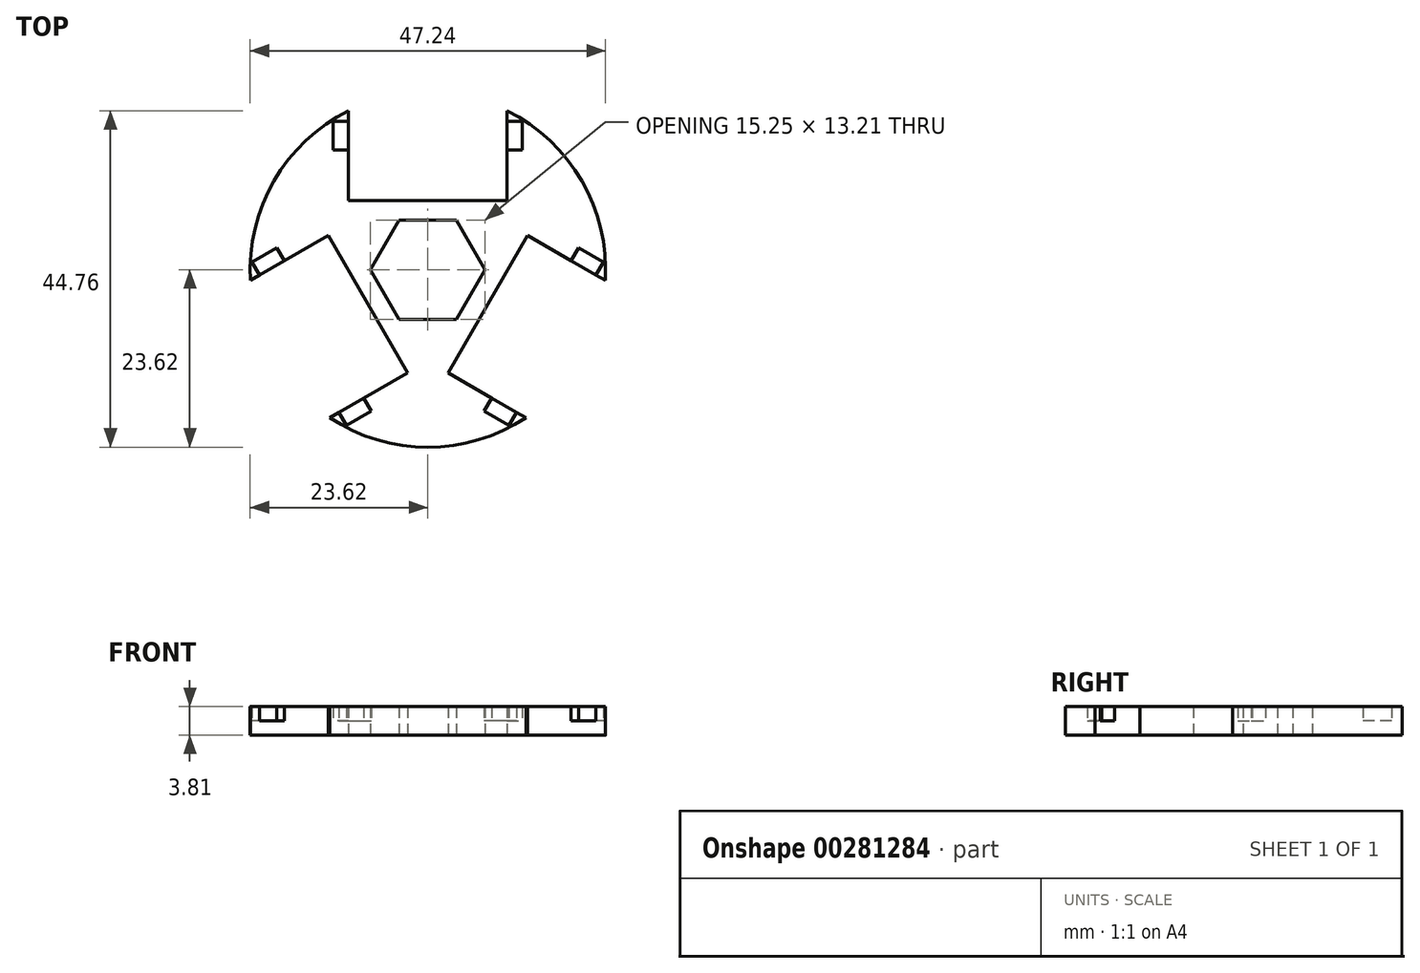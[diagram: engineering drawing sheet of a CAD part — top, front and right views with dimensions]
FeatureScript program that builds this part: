
annotation { "Feature Type Name" : "Feature", "Feature Type Description" : "" }
export const myFeature = defineFeature(function(context is Context, id is Id, definition is map)
    precondition{}
    {
        {
            var Q0;
            Q0=qCreatedBy(makeId("Top.planeOp"),FACE);
            var sketch = newSketch(context, id + "F0", { "sketchPlane" : qUnion([Q0])});
            skCircle(sketch, "E0.cCircle", {"center": v(0, 0) * mm, "radius": 6.6 * mm, "construction": true});
            skLineSegment(sketch, "E0.0", {"start": v(-3.81, 6.6) * mm, "end": v(3.81, 6.6) * mm});
            skLineSegment(sketch, "E0.1", {"start": v(3.81, 6.6) * mm, "end": v(7.63, 0) * mm});
            skLineSegment(sketch, "E0.2", {"start": v(7.63, 0) * mm, "end": v(3.81, -6.6) * mm});
            skLineSegment(sketch, "E0.3", {"start": v(3.81, -6.6) * mm, "end": v(-3.81, -6.6) * mm});
            skLineSegment(sketch, "E0.4", {"start": v(-3.81, -6.6) * mm, "end": v(-7.63, 0) * mm});
            skLineSegment(sketch, "E0.5", {"start": v(-7.63, 0) * mm, "end": v(-3.81, 6.6) * mm});
            skPoint(sketch, "E0.0.midPoint", {"position": v(0, 6.6) * mm});
            skCircle(sketch, "E1", {"center": v(0, 0) * mm, "radius": 23.62 * mm});
            skLineSegment(sketch, "E2.bottom", {"start": v(-10.54, 21.14) * mm, "end": v(10.54, 21.14) * mm});
            skLineSegment(sketch, "E2.top", {"start": v(-10.54, 9.2) * mm, "end": v(10.54, 9.2) * mm});
            skPoint(sketch, "E3.endSnap0", {"position": v(0, 21.14) * mm});
            skLineSegment(sketch, "E4.bottom", {"start": v(-10.54, 19.72) * mm, "end": v(-12.57, 19.72) * mm});
            skLineSegment(sketch, "E4.top", {"start": v(-10.54, 15.9) * mm, "end": v(-12.57, 15.9) * mm});
            skLineSegment(sketch, "E4.right", {"start": v(-12.57, 19.72) * mm, "end": v(-12.57, 15.9) * mm});
            skLineSegment(sketch, "E5", {"start": v(10.54, 21.14) * mm, "end": v(10.54, 19.72) * mm});
            skLineSegment(sketch, "E6", {"start": v(10.54, 15.9) * mm, "end": v(10.54, 9.2) * mm});
            skLineSegment(sketch, "E7", {"start": v(-10.54, 19.72) * mm, "end": v(-10.54, 21.14) * mm});
            skLineSegment(sketch, "E8", {"start": v(-10.54, 15.9) * mm, "end": v(-10.54, 9.2) * mm});
            skLineSegment(sketch, "E9.bottom", {"start": v(10.54, 19.72) * mm, "end": v(12.57, 19.72) * mm});
            skLineSegment(sketch, "E9.top", {"start": v(10.54, 15.9) * mm, "end": v(12.57, 15.9) * mm});
            skLineSegment(sketch, "E9.right", {"start": v(12.57, 19.72) * mm, "end": v(12.57, 15.9) * mm});
            skLineSegment(sketch, "E10", {"start": v(-10.54, 15.9) * mm, "end": v(-10.54, 19.72) * mm});
            skLineSegment(sketch, "E11", {"start": v(10.54, 19.72) * mm, "end": v(10.54, 15.9) * mm});
            skPoint(sketch, "E12", {"position": v(15.71, 9.07) * mm});
            skLineSegment(sketch, "E13.1.0", {"start": v(-22.35, -0.73) * mm, "end": v(-23.36, 1.03) * mm});
            skLineSegment(sketch, "E13.1.1", {"start": v(-23.36, 1.03) * mm, "end": v(-20.06, 2.94) * mm});
            skLineSegment(sketch, "E13.1.2", {"start": v(-22.35, -0.73) * mm, "end": v(-19.05, 1.18) * mm});
            skLineSegment(sketch, "E13.1.3", {"start": v(-19.05, 1.18) * mm, "end": v(-20.06, 2.94) * mm});
            skLineSegment(sketch, "E13.1.4", {"start": v(-19.05, 1.18) * mm, "end": v(-13.24, 4.53) * mm});
            skLineSegment(sketch, "E13.1.5", {"start": v(-2.7, -13.73) * mm, "end": v(-13.24, 4.53) * mm});
            skLineSegment(sketch, "E13.1.6", {"start": v(-8.5, -17.08) * mm, "end": v(-2.7, -13.73) * mm});
            skLineSegment(sketch, "E13.1.7", {"start": v(-8.5, -17.08) * mm, "end": v(-7.49, -18.84) * mm});
            skLineSegment(sketch, "E13.1.8", {"start": v(-8.5, -17.08) * mm, "end": v(-11.8, -18.99) * mm});
            skLineSegment(sketch, "E13.1.9", {"start": v(-11.8, -18.99) * mm, "end": v(-10.79, -20.75) * mm});
            skLineSegment(sketch, "E13.1.10", {"start": v(-10.79, -20.75) * mm, "end": v(-7.49, -18.84) * mm});
            skLineSegment(sketch, "E13.1.11", {"start": v(-11.8, -18.99) * mm, "end": v(-13.04, -19.7) * mm});
            skLineSegment(sketch, "E13.1.12", {"start": v(-13.04, -19.7) * mm, "end": v(-23.58, -1.44) * mm});
            skLineSegment(sketch, "E13.1.13", {"start": v(-23.58, -1.44) * mm, "end": v(-22.35, -0.73) * mm});
            skPoint(sketch, "E13.1.14", {"position": v(-15.71, 9.07) * mm});
            skLineSegment(sketch, "E13.2.0", {"start": v(11.8, -18.99) * mm, "end": v(10.79, -20.75) * mm});
            skLineSegment(sketch, "E13.2.1", {"start": v(10.79, -20.75) * mm, "end": v(7.49, -18.84) * mm});
            skLineSegment(sketch, "E13.2.2", {"start": v(11.8, -18.99) * mm, "end": v(8.5, -17.08) * mm});
            skLineSegment(sketch, "E13.2.3", {"start": v(8.5, -17.08) * mm, "end": v(7.49, -18.84) * mm});
            skLineSegment(sketch, "E13.2.4", {"start": v(8.5, -17.08) * mm, "end": v(2.7, -13.73) * mm});
            skLineSegment(sketch, "E13.2.5", {"start": v(13.24, 4.53) * mm, "end": v(2.7, -13.73) * mm});
            skLineSegment(sketch, "E13.2.6", {"start": v(19.05, 1.18) * mm, "end": v(13.24, 4.53) * mm});
            skLineSegment(sketch, "E13.2.7", {"start": v(19.05, 1.18) * mm, "end": v(20.06, 2.94) * mm});
            skLineSegment(sketch, "E13.2.8", {"start": v(19.05, 1.18) * mm, "end": v(22.35, -0.73) * mm});
            skLineSegment(sketch, "E13.2.9", {"start": v(22.35, -0.73) * mm, "end": v(23.36, 1.03) * mm});
            skLineSegment(sketch, "E13.2.10", {"start": v(23.36, 1.03) * mm, "end": v(20.06, 2.94) * mm});
            skLineSegment(sketch, "E13.2.11", {"start": v(22.35, -0.73) * mm, "end": v(23.58, -1.44) * mm});
            skLineSegment(sketch, "E13.2.12", {"start": v(23.58, -1.44) * mm, "end": v(13.04, -19.7) * mm});
            skLineSegment(sketch, "E13.2.13", {"start": v(13.04, -19.7) * mm, "end": v(11.8, -18.99) * mm});
            skPoint(sketch, "E13.2.14", {"position": v(0, -18.14) * mm});
            skCircle(sketch, "E14.cCircle", {"center": v(0, 0) * mm, "radius": 9.2 * mm, "construction": true});
            skLineSegment(sketch, "E14.0", {"start": v(-5.31, -9.2) * mm, "end": v(-10.63, 0) * mm});
            skLineSegment(sketch, "E14.1", {"start": v(-10.63, 0) * mm, "end": v(-5.31, 9.2) * mm});
            skLineSegment(sketch, "E14.2", {"start": v(-5.31, 9.2) * mm, "end": v(5.31, 9.2) * mm});
            skLineSegment(sketch, "E14.3", {"start": v(5.31, 9.2) * mm, "end": v(10.63, 0) * mm});
            skLineSegment(sketch, "E14.4", {"start": v(10.63, 0) * mm, "end": v(5.31, -9.2) * mm});
            skLineSegment(sketch, "E14.5", {"start": v(5.31, -9.2) * mm, "end": v(-5.31, -9.2) * mm});
            skPoint(sketch, "E14.0.midPoint", {"position": v(-7.97, -4.6) * mm});
            skSolve(sketch);
        }
        {
            var Q0;
            Q0=makeQuery(id+"F0.imprint","IMPRINT",FACE,{"disambiguationData":[TD([[makeQuery(id+"F0.imprint","IMPRINT",EDGE,{"derivedFrom":sQuery(id+"F0.wireOp",EDGE,"E4.bottom")}),-1.0]])]});
            var Q1;
            Q1=makeQuery(id+"F0.imprint","IMPRINT",FACE,{"disambiguationData":[TD([[makeQuery(id+"F0.imprint","IMPRINT",EDGE,{"derivedFrom":sQuery(id+"F0.wireOp",EDGE,"E0.0")}),1.0]])]});
            var Q2;
            {var subQ3=sQuery(id+"F0.wireOp",EDGE,"E5");Q2=makeQuery(id+"F0.imprint","IMPRINT",FACE,{"disambiguationData":[TD([[makeQuery(id+"F0.imprint","IMPRINT",EDGE,{"derivedFrom":subQ3}),1.0]])]});}
            var Q3;
            {var subQ4=sQuery(id+"F0.wireOp",EDGE,"E13.1.6");Q3=makeQuery(id+"F0.imprint","IMPRINT",FACE,{"disambiguationData":[TD([[makeQuery(id+"F0.imprint","IMPRINT",EDGE,{"derivedFrom":subQ4}),-1.0]])]});}
            extrude(context, id + "F1", {"entities" : qUnion([Q0, Q1, Q2, Q3]), "depth" : 3.8 * mm});
        }
        {
            var Q0;
            {var subQ3=sQuery(id+"F0.wireOp",EDGE,"E5");Q0=makeQuery(id+"F0.imprint","IMPRINT",FACE,{"disambiguationData":[TD([[makeQuery(id+"F0.imprint","IMPRINT",EDGE,{"derivedFrom":subQ3}),1.0]])]});}
            var Q1;
            {var subQ4=sQuery(id+"F0.wireOp",EDGE,"E13.1.6");Q1=makeQuery(id+"F0.imprint","IMPRINT",FACE,{"disambiguationData":[TD([[makeQuery(id+"F0.imprint","IMPRINT",EDGE,{"derivedFrom":subQ4}),-1.0]])]});}
            var Q2;
            Q2=makeQuery(id+"F0.imprint","IMPRINT",FACE,{"disambiguationData":[TD([[makeQuery(id+"F0.imprint","IMPRINT",EDGE,{"derivedFrom":sQuery(id+"F0.wireOp",EDGE,"E4.bottom")}),-1.0]])]});
            var Q3;
            Q3=makeQuery(id+"F0.imprint","IMPRINT",FACE,{"disambiguationData":[TD([[makeQuery(id+"F0.imprint","IMPRINT",EDGE,{"derivedFrom":sQuery(id+"F0.wireOp",EDGE,"E13.1.0")}),-1.0]])]});
            var Q4;
            Q4=makeQuery(id+"F0.imprint","IMPRINT",FACE,{"disambiguationData":[TD([[makeQuery(id+"F0.imprint","IMPRINT",EDGE,{"derivedFrom":sQuery(id+"F0.wireOp",EDGE,"E13.1.7")}),-1.0]])]});
            var Q5;
            Q5=makeQuery(id+"F0.imprint","IMPRINT",FACE,{"disambiguationData":[TD([[makeQuery(id+"F0.imprint","IMPRINT",EDGE,{"derivedFrom":sQuery(id+"F0.wireOp",EDGE,"E13.2.0")}),-1.0]])]});
            var Q6;
            Q6=makeQuery(id+"F0.imprint","IMPRINT",FACE,{"disambiguationData":[TD([[makeQuery(id+"F0.imprint","IMPRINT",EDGE,{"derivedFrom":sQuery(id+"F0.wireOp",EDGE,"E13.2.7")}),-1.0]])]});
            var Q7;
            Q7=makeQuery(id+"F0.imprint","IMPRINT",FACE,{"disambiguationData":[TD([[makeQuery(id+"F0.imprint","IMPRINT",EDGE,{"derivedFrom":sQuery(id+"F0.wireOp",EDGE,"E4.bottom")}),1.0]])]});
            var Q8;
            Q8=makeQuery(id+"F0.imprint","IMPRINT",FACE,{"disambiguationData":[TD([[makeQuery(id+"F0.imprint","IMPRINT",EDGE,{"derivedFrom":sQuery(id+"F0.wireOp",EDGE,"E9.bottom")}),-1.0]])]});
            extrude(context, id + "F2", {"entities" : qUnion([Q0, Q1, Q2, Q3, Q4, Q5, Q6, Q7, Q8]), "operationType" : NewBodyOperationType.ADD, "depth" : 1.9 * mm});
        }
    });
